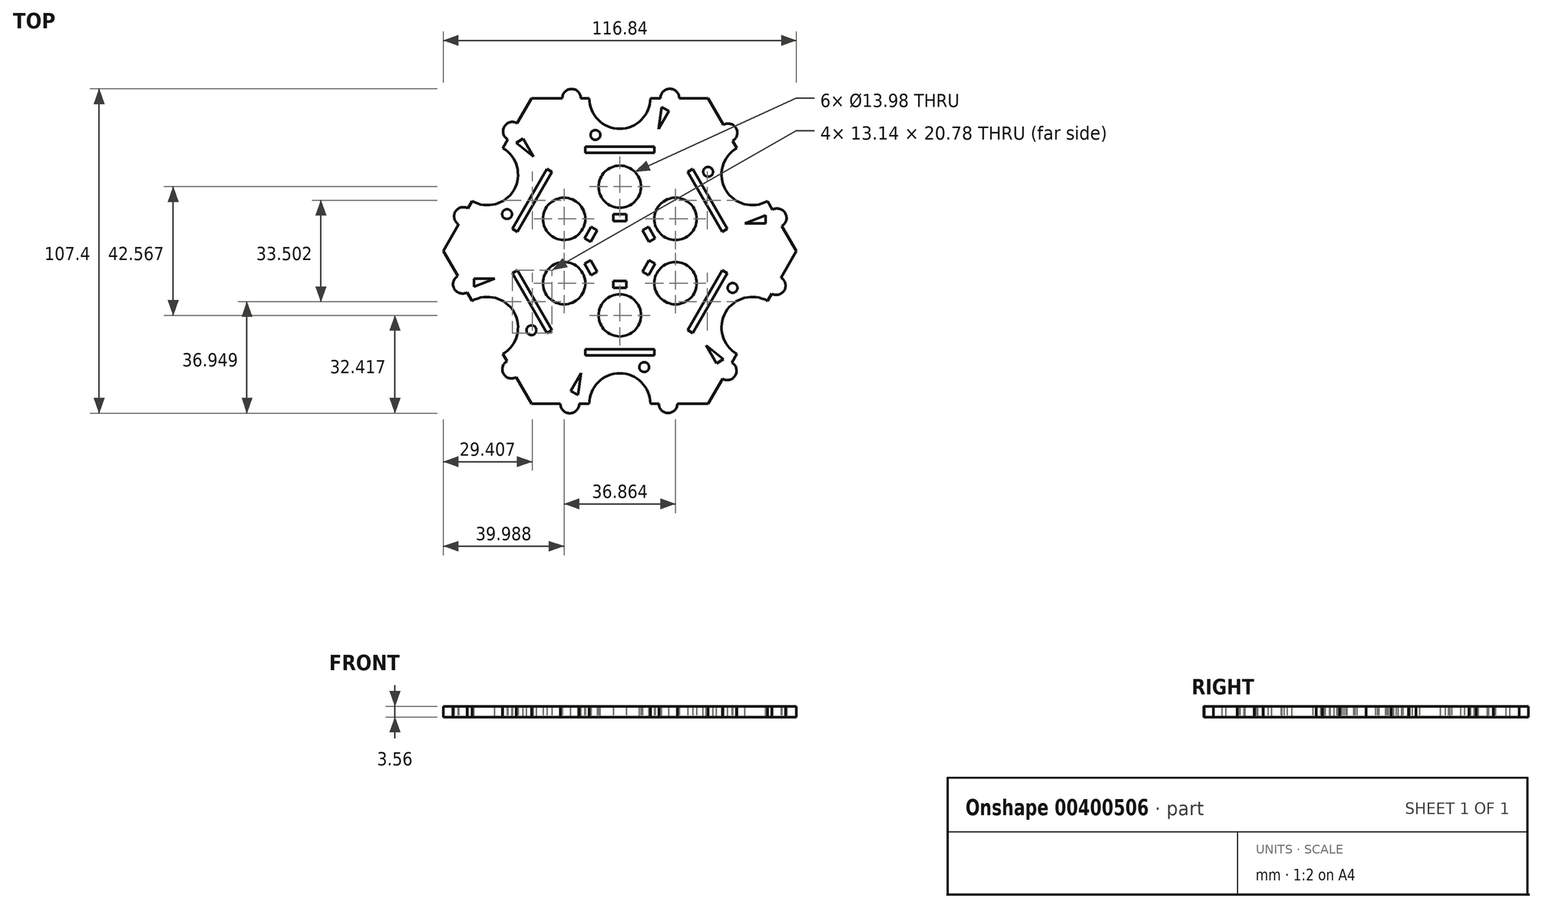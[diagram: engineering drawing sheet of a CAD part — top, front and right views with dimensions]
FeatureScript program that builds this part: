
annotation { "Feature Type Name" : "Feature", "Feature Type Description" : "" }
export const myFeature = defineFeature(function(context is Context, id is Id, definition is map)
    precondition{}
    {
        {
            var Q0;
            Q0=qCreatedBy(makeId("Top.planeOp"),FACE);
            var sketch = newSketch(context, id + "F0", { "sketchPlane" : qUnion([Q0])});
            skLineSegment(sketch, "E0", {"start": v(0, 0) * mm, "end": v(-29.21, -50.6) * mm});
            skLineSegment(sketch, "E1", {"start": v(-29.21, -50.6) * mm, "end": v(-19.66, -50.6) * mm});
            skLineSegment(sketch, "E2", {"start": v(29.21, -50.6) * mm, "end": v(0, 0) * mm});
            skArc(sketch, "E3", {"start": v(10.12, -50.6) * mm, "mid": v(0, -40.48) * mm, "end": v(-10.12, -50.6) * mm});
            skArc(sketch, "E4", {"start": v(12.9, -50.6) * mm, "mid": v(15.96, -53.65) * mm, "end": v(19.02, -50.6) * mm});
            skArc(sketch, "E5", {"start": v(-19.66, -50.6) * mm, "mid": v(-16.55, -53.7) * mm, "end": v(-13.44, -50.6) * mm});
            skCircle(sketch, "E6", {"center": v(0, -21.28) * mm, "radius": 7 * mm});
            skLineSegment(sketch, "E7.bottom", {"start": v(11.43, -34.49) * mm, "end": v(-11.43, -34.49) * mm});
            skLineSegment(sketch, "E7.top", {"start": v(11.43, -32.52) * mm, "end": v(-11.43, -32.52) * mm});
            skLineSegment(sketch, "E7.left", {"start": v(11.43, -34.49) * mm, "end": v(11.43, -32.52) * mm});
            skLineSegment(sketch, "E7.right", {"start": v(-11.43, -34.49) * mm, "end": v(-11.43, -32.52) * mm});
            skPoint(sketch, "E7.middle", {"position": v(0, -33.5) * mm});
            skLineSegment(sketch, "E8.bottom", {"start": v(2.17, -12.22) * mm, "end": v(-2.17, -12.22) * mm});
            skLineSegment(sketch, "E8.top", {"start": v(2.17, -9.85) * mm, "end": v(-2.17, -9.85) * mm});
            skLineSegment(sketch, "E8.left", {"start": v(2.17, -12.22) * mm, "end": v(2.17, -9.85) * mm});
            skLineSegment(sketch, "E8.right", {"start": v(-2.17, -12.22) * mm, "end": v(-2.17, -9.85) * mm});
            skPoint(sketch, "E8.middle", {"position": v(0, -11.04) * mm});
            skLineSegment(sketch, "E9.trimOffspring", {"start": v(10.12, -50.6) * mm, "end": v(12.9, -50.6) * mm});
            skLineSegment(sketch, "E10.trimOffspring", {"start": v(19.02, -50.6) * mm, "end": v(29.21, -50.6) * mm});
            skLineSegment(sketch, "E11.trimOffspring", {"start": v(-13.44, -50.6) * mm, "end": v(-10.12, -50.6) * mm});
            skArc(sketch, "E12.1.0", {"start": v(-37.36, -36.48) * mm, "mid": v(-38.48, -40.65) * mm, "end": v(-34.3, -41.77) * mm});
            skPoint(sketch, "E12.1.1", {"position": v(-29.01, -16.75) * mm});
            skArc(sketch, "E12.1.2", {"start": v(-53.65, -8.27) * mm, "mid": v(-54.78, -12.52) * mm, "end": v(-50.54, -13.65) * mm});
            skArc(sketch, "E12.1.3", {"start": v(-38.76, -34.06) * mm, "mid": v(-35.05, -20.24) * mm, "end": v(-48.87, -16.53) * mm});
            skCircle(sketch, "E12.1.4", {"center": v(-18.43, -10.64) * mm, "radius": 7 * mm});
            skLineSegment(sketch, "E12.1.5", {"start": v(-29.21, -50.6) * mm, "end": v(0, 0) * mm});
            skLineSegment(sketch, "E12.1.6", {"start": v(-24.15, -27.14) * mm, "end": v(-35.58, -7.34) * mm});
            skLineSegment(sketch, "E12.1.7", {"start": v(-58.42, 0) * mm, "end": v(-53.65, -8.27) * mm});
            skLineSegment(sketch, "E12.1.8", {"start": v(-22.45, -26.16) * mm, "end": v(-33.88, -6.36) * mm});
            skLineSegment(sketch, "E12.1.9", {"start": v(0, 0) * mm, "end": v(-58.42, 0) * mm});
            skLineSegment(sketch, "E12.1.10", {"start": v(-38.76, -34.06) * mm, "end": v(-37.36, -36.48) * mm});
            skLineSegment(sketch, "E12.1.11", {"start": v(-50.54, -13.65) * mm, "end": v(-48.87, -16.53) * mm});
            skPoint(sketch, "E12.1.12", {"position": v(-9.56, -5.52) * mm});
            skLineSegment(sketch, "E12.1.13", {"start": v(-34.3, -41.77) * mm, "end": v(-29.21, -50.6) * mm});
            skLineSegment(sketch, "E12.1.14", {"start": v(-24.15, -27.14) * mm, "end": v(-22.45, -26.16) * mm});
            skLineSegment(sketch, "E12.1.15", {"start": v(-35.58, -7.34) * mm, "end": v(-33.88, -6.36) * mm});
            skLineSegment(sketch, "E12.1.16", {"start": v(-7.45, -6.8) * mm, "end": v(-9.62, -3.05) * mm});
            skLineSegment(sketch, "E12.1.17", {"start": v(-11.67, -4.23) * mm, "end": v(-9.62, -3.05) * mm});
            skLineSegment(sketch, "E12.1.18", {"start": v(-9.5, -7.99) * mm, "end": v(-7.45, -6.8) * mm});
            skLineSegment(sketch, "E12.1.19", {"start": v(-9.5, -7.99) * mm, "end": v(-11.67, -4.23) * mm});
            skArc(sketch, "E12.2.0", {"start": v(-50.27, 14.12) * mm, "mid": v(-54.44, 13) * mm, "end": v(-53.32, 8.83) * mm});
            skPoint(sketch, "E12.2.1", {"position": v(-29.01, 16.75) * mm});
            skArc(sketch, "E12.2.2", {"start": v(-33.98, 42.33) * mm, "mid": v(-38.23, 41.19) * mm, "end": v(-37.1, 36.94) * mm});
            skArc(sketch, "E12.2.3", {"start": v(-48.87, 16.53) * mm, "mid": v(-35.05, 20.24) * mm, "end": v(-38.76, 34.06) * mm});
            skCircle(sketch, "E12.2.4", {"center": v(-18.43, 10.64) * mm, "radius": 7 * mm});
            skLineSegment(sketch, "E12.2.5", {"start": v(-58.42, 0) * mm, "end": v(0, 0) * mm});
            skLineSegment(sketch, "E12.2.6", {"start": v(-35.58, 7.34) * mm, "end": v(-24.15, 27.14) * mm});
            skLineSegment(sketch, "E12.2.7", {"start": v(-29.21, 50.6) * mm, "end": v(-33.98, 42.33) * mm});
            skLineSegment(sketch, "E12.2.8", {"start": v(-33.88, 6.36) * mm, "end": v(-22.45, 26.16) * mm});
            skLineSegment(sketch, "E12.2.9", {"start": v(0, 0) * mm, "end": v(-29.21, 50.6) * mm});
            skLineSegment(sketch, "E12.2.10", {"start": v(-48.87, 16.53) * mm, "end": v(-50.27, 14.12) * mm});
            skLineSegment(sketch, "E12.2.11", {"start": v(-37.1, 36.94) * mm, "end": v(-38.76, 34.06) * mm});
            skPoint(sketch, "E12.2.12", {"position": v(-9.56, 5.52) * mm});
            skLineSegment(sketch, "E12.2.13", {"start": v(-53.32, 8.83) * mm, "end": v(-58.42, 0) * mm});
            skLineSegment(sketch, "E12.2.14", {"start": v(-35.58, 7.34) * mm, "end": v(-33.88, 6.36) * mm});
            skLineSegment(sketch, "E12.2.15", {"start": v(-24.15, 27.14) * mm, "end": v(-22.45, 26.16) * mm});
            skLineSegment(sketch, "E12.2.16", {"start": v(-9.62, 3.05) * mm, "end": v(-7.45, 6.8) * mm});
            skLineSegment(sketch, "E12.2.17", {"start": v(-9.5, 7.99) * mm, "end": v(-7.45, 6.8) * mm});
            skLineSegment(sketch, "E12.2.18", {"start": v(-11.67, 4.23) * mm, "end": v(-9.62, 3.05) * mm});
            skLineSegment(sketch, "E12.2.19", {"start": v(-11.67, 4.23) * mm, "end": v(-9.5, 7.99) * mm});
            skArc(sketch, "E12.3.0", {"start": v(-12.9, 50.6) * mm, "mid": v(-15.96, 53.65) * mm, "end": v(-19.02, 50.6) * mm});
            skPoint(sketch, "E12.3.1", {"position": v(0, 33.5) * mm});
            skArc(sketch, "E12.3.2", {"start": v(19.66, 50.6) * mm, "mid": v(16.55, 53.7) * mm, "end": v(13.44, 50.6) * mm});
            skArc(sketch, "E12.3.3", {"start": v(-10.12, 50.6) * mm, "mid": v(0, 40.48) * mm, "end": v(10.12, 50.6) * mm});
            skCircle(sketch, "E12.3.4", {"center": v(0, 21.28) * mm, "radius": 7 * mm});
            skLineSegment(sketch, "E12.3.5", {"start": v(-29.21, 50.6) * mm, "end": v(0, 0) * mm});
            skLineSegment(sketch, "E12.3.6", {"start": v(-11.43, 34.49) * mm, "end": v(11.43, 34.49) * mm});
            skLineSegment(sketch, "E12.3.7", {"start": v(29.21, 50.6) * mm, "end": v(19.66, 50.6) * mm});
            skLineSegment(sketch, "E12.3.8", {"start": v(-11.43, 32.52) * mm, "end": v(11.43, 32.52) * mm});
            skLineSegment(sketch, "E12.3.9", {"start": v(0, 0) * mm, "end": v(29.21, 50.6) * mm});
            skLineSegment(sketch, "E12.3.10", {"start": v(-10.12, 50.6) * mm, "end": v(-12.9, 50.6) * mm});
            skLineSegment(sketch, "E12.3.11", {"start": v(13.44, 50.6) * mm, "end": v(10.12, 50.6) * mm});
            skPoint(sketch, "E12.3.12", {"position": v(0, 11.04) * mm});
            skLineSegment(sketch, "E12.3.13", {"start": v(-19.02, 50.6) * mm, "end": v(-29.21, 50.6) * mm});
            skLineSegment(sketch, "E12.3.14", {"start": v(-11.43, 34.49) * mm, "end": v(-11.43, 32.52) * mm});
            skLineSegment(sketch, "E12.3.15", {"start": v(11.43, 34.49) * mm, "end": v(11.43, 32.52) * mm});
            skLineSegment(sketch, "E12.3.16", {"start": v(-2.17, 9.85) * mm, "end": v(2.17, 9.85) * mm});
            skLineSegment(sketch, "E12.3.17", {"start": v(2.17, 12.22) * mm, "end": v(2.17, 9.85) * mm});
            skLineSegment(sketch, "E12.3.18", {"start": v(-2.17, 12.22) * mm, "end": v(-2.17, 9.85) * mm});
            skLineSegment(sketch, "E12.3.19", {"start": v(-2.17, 12.22) * mm, "end": v(2.17, 12.22) * mm});
            skArc(sketch, "E12.4.0", {"start": v(37.36, 36.48) * mm, "mid": v(38.48, 40.65) * mm, "end": v(34.3, 41.77) * mm});
            skPoint(sketch, "E12.4.1", {"position": v(29.01, 16.75) * mm});
            skArc(sketch, "E12.4.2", {"start": v(53.65, 8.27) * mm, "mid": v(54.78, 12.52) * mm, "end": v(50.54, 13.65) * mm});
            skArc(sketch, "E12.4.3", {"start": v(38.76, 34.06) * mm, "mid": v(35.05, 20.24) * mm, "end": v(48.87, 16.53) * mm});
            skCircle(sketch, "E12.4.4", {"center": v(18.43, 10.64) * mm, "radius": 7 * mm});
            skLineSegment(sketch, "E12.4.5", {"start": v(29.21, 50.6) * mm, "end": v(0, 0) * mm});
            skLineSegment(sketch, "E12.4.6", {"start": v(24.15, 27.14) * mm, "end": v(35.58, 7.34) * mm});
            skLineSegment(sketch, "E12.4.7", {"start": v(58.42, 0) * mm, "end": v(53.65, 8.27) * mm});
            skLineSegment(sketch, "E12.4.8", {"start": v(22.45, 26.16) * mm, "end": v(33.88, 6.36) * mm});
            skLineSegment(sketch, "E12.4.9", {"start": v(0, 0) * mm, "end": v(58.42, 0) * mm});
            skLineSegment(sketch, "E12.4.10", {"start": v(38.76, 34.06) * mm, "end": v(37.36, 36.48) * mm});
            skLineSegment(sketch, "E12.4.11", {"start": v(50.54, 13.65) * mm, "end": v(48.87, 16.53) * mm});
            skPoint(sketch, "E12.4.12", {"position": v(9.56, 5.52) * mm});
            skLineSegment(sketch, "E12.4.13", {"start": v(34.3, 41.77) * mm, "end": v(29.21, 50.6) * mm});
            skLineSegment(sketch, "E12.4.14", {"start": v(24.15, 27.14) * mm, "end": v(22.45, 26.16) * mm});
            skLineSegment(sketch, "E12.4.15", {"start": v(35.58, 7.34) * mm, "end": v(33.88, 6.36) * mm});
            skLineSegment(sketch, "E12.4.16", {"start": v(7.45, 6.8) * mm, "end": v(9.62, 3.05) * mm});
            skLineSegment(sketch, "E12.4.17", {"start": v(11.67, 4.23) * mm, "end": v(9.62, 3.05) * mm});
            skLineSegment(sketch, "E12.4.18", {"start": v(9.5, 7.99) * mm, "end": v(7.45, 6.8) * mm});
            skLineSegment(sketch, "E12.4.19", {"start": v(9.5, 7.99) * mm, "end": v(11.67, 4.23) * mm});
            skArc(sketch, "E12.5.0", {"start": v(50.27, -14.12) * mm, "mid": v(54.44, -13) * mm, "end": v(53.32, -8.83) * mm});
            skPoint(sketch, "E12.5.1", {"position": v(29.01, -16.75) * mm});
            skArc(sketch, "E12.5.2", {"start": v(33.98, -42.33) * mm, "mid": v(38.23, -41.19) * mm, "end": v(37.1, -36.94) * mm});
            skArc(sketch, "E12.5.3", {"start": v(48.87, -16.53) * mm, "mid": v(35.05, -20.24) * mm, "end": v(38.76, -34.06) * mm});
            skCircle(sketch, "E12.5.4", {"center": v(18.43, -10.64) * mm, "radius": 7 * mm});
            skLineSegment(sketch, "E12.5.5", {"start": v(58.42, 0) * mm, "end": v(0, 0) * mm});
            skLineSegment(sketch, "E12.5.6", {"start": v(35.58, -7.34) * mm, "end": v(24.15, -27.14) * mm});
            skLineSegment(sketch, "E12.5.7", {"start": v(29.21, -50.6) * mm, "end": v(33.98, -42.33) * mm});
            skLineSegment(sketch, "E12.5.8", {"start": v(33.88, -6.36) * mm, "end": v(22.45, -26.16) * mm});
            skLineSegment(sketch, "E12.5.9", {"start": v(0, 0) * mm, "end": v(29.21, -50.6) * mm});
            skLineSegment(sketch, "E12.5.10", {"start": v(48.87, -16.53) * mm, "end": v(50.27, -14.12) * mm});
            skLineSegment(sketch, "E12.5.11", {"start": v(37.1, -36.94) * mm, "end": v(38.76, -34.06) * mm});
            skPoint(sketch, "E12.5.12", {"position": v(9.56, -5.52) * mm});
            skLineSegment(sketch, "E12.5.13", {"start": v(53.32, -8.83) * mm, "end": v(58.42, 0) * mm});
            skLineSegment(sketch, "E12.5.14", {"start": v(35.58, -7.34) * mm, "end": v(33.88, -6.36) * mm});
            skLineSegment(sketch, "E12.5.15", {"start": v(24.15, -27.14) * mm, "end": v(22.45, -26.16) * mm});
            skLineSegment(sketch, "E12.5.16", {"start": v(9.62, -3.05) * mm, "end": v(7.45, -6.8) * mm});
            skLineSegment(sketch, "E12.5.17", {"start": v(9.5, -7.99) * mm, "end": v(7.45, -6.8) * mm});
            skLineSegment(sketch, "E12.5.18", {"start": v(11.67, -4.23) * mm, "end": v(9.62, -3.05) * mm});
            skLineSegment(sketch, "E12.5.19", {"start": v(11.67, -4.23) * mm, "end": v(9.5, -7.99) * mm});
            skPoint(sketch, "E12.center", {"position": v(0, 0) * mm});
            skLineSegment(sketch, "E12.anchor1", {"start": v(0, 0) * mm, "end": v(-29.21, -50.6) * mm, "construction": true});
            skLineSegment(sketch, "E12.anchor2", {"start": v(0, 0) * mm, "end": v(29.21, -50.6) * mm, "construction": true});
            skSolve(sketch);
        }
        {
            var Q0;
            Q0=makeQuery(id+"F0.imprint","IMPRINT",FACE,{"disambiguationData":[TD([[makeQuery(id+"F0.imprint","IMPRINT",EDGE,{"derivedFrom":sQuery(id+"F0.wireOp",EDGE,"E12.2.0")}),1.0]])]});
            var Q1;
            Q1=makeQuery(id+"F0.imprint","IMPRINT",FACE,{"disambiguationData":[TD([[makeQuery(id+"F0.imprint","IMPRINT",EDGE,{"derivedFrom":sQuery(id+"F0.wireOp",EDGE,"E12.1.0")}),1.0]])]});
            var Q2;
            Q2=makeQuery(id+"F0.imprint","IMPRINT",FACE,{"disambiguationData":[TD([[makeQuery(id+"F0.imprint","IMPRINT",EDGE,{"derivedFrom":sQuery(id+"F0.wireOp",EDGE,"E12.3.0")}),1.0]])]});
            var Q3;
            Q3=makeQuery(id+"F0.imprint","IMPRINT",FACE,{"disambiguationData":[TD([[makeQuery(id+"F0.imprint","IMPRINT",EDGE,{"derivedFrom":sQuery(id+"F0.wireOp",EDGE,"E12.4.0")}),1.0]])]});
            var Q4;
            Q4=makeQuery(id+"F0.imprint","IMPRINT",FACE,{"disambiguationData":[TD([[makeQuery(id+"F0.imprint","IMPRINT",EDGE,{"derivedFrom":sQuery(id+"F0.wireOp",EDGE,"E12.5.0")}),1.0]])]});
            var Q5;
            Q5=makeQuery(id+"F0.imprint","IMPRINT",FACE,{"disambiguationData":[TD([[makeQuery(id+"F0.imprint","IMPRINT",EDGE,{"derivedFrom":sQuery(id+"F0.wireOp",EDGE,"E1")}),1.0]])]});
            extrude(context, id + "F1", {"entities" : qUnion([Q0, Q1, Q2, Q3, Q4, Q5]), "depth" : 3.56 * mm});
        }
        {
            var Q0;
            Q0=makeQuery(id+"F1.opExtrude","CAP_FACE",FACE,{"disambiguationData":[OSD([sQuery(id+"F0.wireOp",EDGE,"E1"),sQuery(id+"F0.wireOp",EDGE,"E3"),sQuery(id+"F0.wireOp",EDGE,"E4"),sQuery(id+"F0.wireOp",EDGE,"E5"),sQuery(id+"F0.wireOp",EDGE,"E6"),sQuery(id+"F0.wireOp",EDGE,"E7.bottom"),sQuery(id+"F0.wireOp",EDGE,"E7.top"),sQuery(id+"F0.wireOp",EDGE,"E7.left"),sQuery(id+"F0.wireOp",EDGE,"E7.right"),sQuery(id+"F0.wireOp",EDGE,"E8.bottom"),sQuery(id+"F0.wireOp",EDGE,"E8.top"),sQuery(id+"F0.wireOp",EDGE,"E8.left"),sQuery(id+"F0.wireOp",EDGE,"E8.right"),sQuery(id+"F0.wireOp",EDGE,"E9.trimOffspring"),sQuery(id+"F0.wireOp",EDGE,"E10.trimOffspring"),sQuery(id+"F0.wireOp",EDGE,"E11.trimOffspring"),sQuery(id+"F0.wireOp",EDGE,"E12.1.0"),sQuery(id+"F0.wireOp",EDGE,"E12.1.2"),sQuery(id+"F0.wireOp",EDGE,"E12.1.3"),sQuery(id+"F0.wireOp",EDGE,"E12.1.4"),sQuery(id+"F0.wireOp",EDGE,"E12.1.6"),sQuery(id+"F0.wireOp",EDGE,"E12.1.7"),sQuery(id+"F0.wireOp",EDGE,"E12.1.8"),sQuery(id+"F0.wireOp",EDGE,"E12.1.10"),sQuery(id+"F0.wireOp",EDGE,"E12.1.11"),sQuery(id+"F0.wireOp",EDGE,"E12.1.13"),sQuery(id+"F0.wireOp",EDGE,"E12.1.14"),sQuery(id+"F0.wireOp",EDGE,"E12.1.15"),sQuery(id+"F0.wireOp",EDGE,"E12.1.16"),sQuery(id+"F0.wireOp",EDGE,"E12.1.17"),sQuery(id+"F0.wireOp",EDGE,"E12.1.18"),sQuery(id+"F0.wireOp",EDGE,"E12.1.19"),sQuery(id+"F0.wireOp",EDGE,"E12.2.0"),sQuery(id+"F0.wireOp",EDGE,"E12.2.2"),sQuery(id+"F0.wireOp",EDGE,"E12.2.3"),sQuery(id+"F0.wireOp",EDGE,"E12.2.4"),sQuery(id+"F0.wireOp",EDGE,"E12.2.6"),sQuery(id+"F0.wireOp",EDGE,"E12.2.7"),sQuery(id+"F0.wireOp",EDGE,"E12.2.8"),sQuery(id+"F0.wireOp",EDGE,"E12.2.10"),sQuery(id+"F0.wireOp",EDGE,"E12.2.11"),sQuery(id+"F0.wireOp",EDGE,"E12.2.13"),sQuery(id+"F0.wireOp",EDGE,"E12.2.14"),sQuery(id+"F0.wireOp",EDGE,"E12.2.15"),sQuery(id+"F0.wireOp",EDGE,"E12.2.16"),sQuery(id+"F0.wireOp",EDGE,"E12.2.17"),sQuery(id+"F0.wireOp",EDGE,"E12.2.18"),sQuery(id+"F0.wireOp",EDGE,"E12.2.19"),sQuery(id+"F0.wireOp",EDGE,"E12.3.0"),sQuery(id+"F0.wireOp",EDGE,"E12.3.2"),sQuery(id+"F0.wireOp",EDGE,"E12.3.3"),sQuery(id+"F0.wireOp",EDGE,"E12.3.4"),sQuery(id+"F0.wireOp",EDGE,"E12.3.6"),sQuery(id+"F0.wireOp",EDGE,"E12.3.7"),sQuery(id+"F0.wireOp",EDGE,"E12.3.8"),sQuery(id+"F0.wireOp",EDGE,"E12.3.10"),sQuery(id+"F0.wireOp",EDGE,"E12.3.11"),sQuery(id+"F0.wireOp",EDGE,"E12.3.13"),sQuery(id+"F0.wireOp",EDGE,"E12.3.14"),sQuery(id+"F0.wireOp",EDGE,"E12.3.15"),sQuery(id+"F0.wireOp",EDGE,"E12.3.16"),sQuery(id+"F0.wireOp",EDGE,"E12.3.17"),sQuery(id+"F0.wireOp",EDGE,"E12.3.18"),sQuery(id+"F0.wireOp",EDGE,"E12.3.19"),sQuery(id+"F0.wireOp",EDGE,"E12.4.0"),sQuery(id+"F0.wireOp",EDGE,"E12.4.2"),sQuery(id+"F0.wireOp",EDGE,"E12.4.3"),sQuery(id+"F0.wireOp",EDGE,"E12.4.4"),sQuery(id+"F0.wireOp",EDGE,"E12.4.6"),sQuery(id+"F0.wireOp",EDGE,"E12.4.7"),sQuery(id+"F0.wireOp",EDGE,"E12.4.8"),sQuery(id+"F0.wireOp",EDGE,"E12.4.10"),sQuery(id+"F0.wireOp",EDGE,"E12.4.11"),sQuery(id+"F0.wireOp",EDGE,"E12.4.13"),sQuery(id+"F0.wireOp",EDGE,"E12.4.14"),sQuery(id+"F0.wireOp",EDGE,"E12.4.15"),sQuery(id+"F0.wireOp",EDGE,"E12.4.16"),sQuery(id+"F0.wireOp",EDGE,"E12.4.17"),sQuery(id+"F0.wireOp",EDGE,"E12.4.18"),sQuery(id+"F0.wireOp",EDGE,"E12.4.19"),sQuery(id+"F0.wireOp",EDGE,"E12.5.0"),sQuery(id+"F0.wireOp",EDGE,"E12.5.2"),sQuery(id+"F0.wireOp",EDGE,"E12.5.3"),sQuery(id+"F0.wireOp",EDGE,"E12.5.4"),sQuery(id+"F0.wireOp",EDGE,"E12.5.6"),sQuery(id+"F0.wireOp",EDGE,"E12.5.7"),sQuery(id+"F0.wireOp",EDGE,"E12.5.8"),sQuery(id+"F0.wireOp",EDGE,"E12.5.10"),sQuery(id+"F0.wireOp",EDGE,"E12.5.11"),sQuery(id+"F0.wireOp",EDGE,"E12.5.13"),sQuery(id+"F0.wireOp",EDGE,"E12.5.14"),sQuery(id+"F0.wireOp",EDGE,"E12.5.15"),sQuery(id+"F0.wireOp",EDGE,"E12.5.16"),sQuery(id+"F0.wireOp",EDGE,"E12.5.17"),sQuery(id+"F0.wireOp",EDGE,"E12.5.18"),sQuery(id+"F0.wireOp",EDGE,"E12.5.19")])],"isStart":false});
            var sketch = newSketch(context, id + "F2", { "sketchPlane" : qUnion([Q0])});
            skCircle(sketch, "E13", {"center": v(8.08, -38.43) * mm, "radius": 1.63 * mm});
            skLineSegment(sketch, "E14", {"start": v(-12.8, -40.4) * mm, "end": v(-16.22, -46.3) * mm});
            skLineSegment(sketch, "E15", {"start": v(-16.22, -46.3) * mm, "end": v(-13.87, -47.66) * mm});
            skLineSegment(sketch, "E16", {"start": v(-13.87, -47.66) * mm, "end": v(-12.8, -40.4) * mm});
            skLineSegment(sketch, "E17.1.0", {"start": v(28.58, -31.3) * mm, "end": v(32, -37.2) * mm});
            skLineSegment(sketch, "E17.1.1", {"start": v(34.34, -35.84) * mm, "end": v(28.58, -31.3) * mm});
            skCircle(sketch, "E17.1.2", {"center": v(37.32, -12.22) * mm, "radius": 1.63 * mm});
            skLineSegment(sketch, "E17.1.3", {"start": v(32, -37.2) * mm, "end": v(34.34, -35.84) * mm});
            skLineSegment(sketch, "E17.2.0", {"start": v(41.4, 9.1) * mm, "end": v(48.21, 9.1) * mm});
            skLineSegment(sketch, "E17.2.1", {"start": v(48.21, 11.82) * mm, "end": v(41.4, 9.1) * mm});
            skCircle(sketch, "E17.2.2", {"center": v(29.24, 26.21) * mm, "radius": 1.63 * mm});
            skLineSegment(sketch, "E17.2.3", {"start": v(48.21, 9.1) * mm, "end": v(48.21, 11.82) * mm});
            skLineSegment(sketch, "E17.3.0", {"start": v(12.8, 40.4) * mm, "end": v(16.22, 46.3) * mm});
            skLineSegment(sketch, "E17.3.1", {"start": v(13.87, 47.66) * mm, "end": v(12.8, 40.4) * mm});
            skCircle(sketch, "E17.3.2", {"center": v(-8.08, 38.43) * mm, "radius": 1.63 * mm});
            skLineSegment(sketch, "E17.3.3", {"start": v(16.22, 46.3) * mm, "end": v(13.87, 47.66) * mm});
            skLineSegment(sketch, "E17.4.0", {"start": v(-28.58, 31.3) * mm, "end": v(-32, 37.2) * mm});
            skLineSegment(sketch, "E17.4.1", {"start": v(-34.34, 35.84) * mm, "end": v(-28.58, 31.3) * mm});
            skCircle(sketch, "E17.4.2", {"center": v(-37.32, 12.22) * mm, "radius": 1.63 * mm});
            skLineSegment(sketch, "E17.4.3", {"start": v(-32, 37.2) * mm, "end": v(-34.34, 35.84) * mm});
            skLineSegment(sketch, "E17.5.0", {"start": v(-41.4, -9.1) * mm, "end": v(-48.21, -9.1) * mm});
            skLineSegment(sketch, "E17.5.1", {"start": v(-48.21, -11.82) * mm, "end": v(-41.4, -9.1) * mm});
            skCircle(sketch, "E17.5.2", {"center": v(-29.24, -26.21) * mm, "radius": 1.63 * mm});
            skLineSegment(sketch, "E17.5.3", {"start": v(-48.21, -9.1) * mm, "end": v(-48.21, -11.82) * mm});
            skPoint(sketch, "E17.center", {"position": v(0, 0) * mm});
            skSolve(sketch);
        }
        {
            var Q0;
            Q0 = qSketchRegion(id + "F2", true);
            extrude(context, id + "F3", {"entities" : qUnion([Q0]), "operationType" : NewBodyOperationType.REMOVE, "oppositeDirection" : true, "depth" : 25.4 * mm});
        }
    });
